# Revit family: CI604ZZDTB5-CI604ZZDTG5-CN
name_source: partatom
category: Specialty Equipment
units: mm (PartAtom-declared; Revit-internal decimal feet)

## family parameters
Always vertical = No
Cut with Voids When Loaded = Yes
Part Type = Normal
Room Calculation Point = No
Round Connector Dimension = Use Diameter
Shared = No
Work Plane-Based = Yes

## types (2) — shared parameters
Cavity - Depth = 490 mm  [stored 1.60761 ft]
Cavity - Height = 2260 mm
Cavity - Width = 560 mm  [stored 1.83727 ft]
Clearance - Below Cooktop = 86 mm  [stored 0.282152 ft]
Clearance - Overhead Rangehood = 650 mm  [stored 2.13255 ft]
Description = 60cm Series 7 Induction Cooktop
Manufacturer = Fisher & Paykel Appliances
Product - Depth = 528 mm  [stored 1.73228 ft]
Product - Height = 90 mm  [stored 0.295276 ft]
Product - Width = 598 mm
URL = www.fisherpaykel.com
zero-valued in all types: Default Elevation

## per-type parameters (varying)
| type | Material - Cooktop |
| CI604ZZDTB5 | Fisher & Paykel - Glass, Black |
| CI604ZZDTG5 | Fisher & Paykel - Glass, Grey |

note: column(s) folded — value = type name in every type: Model

note: [stored X ft] marks values corroborated as IEEE doubles in the binary element streams (Revit-internal decimal feet)

## geometry (parser evidence)
native form markers: Sweep x111
no freeform markers — native parametric forms only
